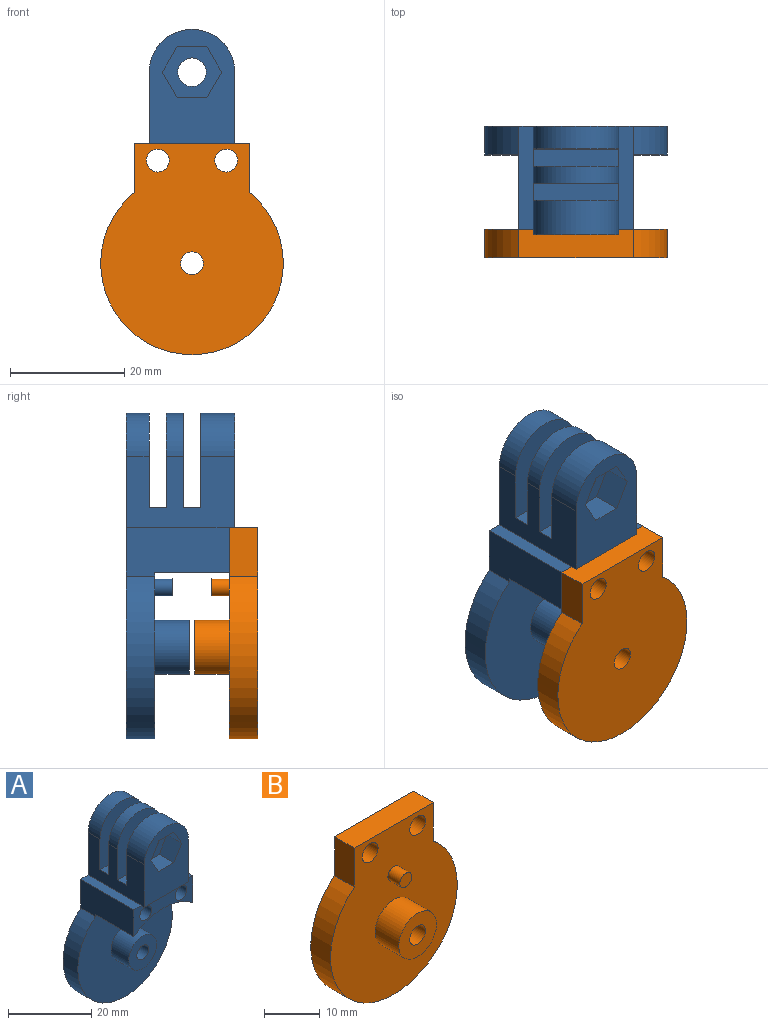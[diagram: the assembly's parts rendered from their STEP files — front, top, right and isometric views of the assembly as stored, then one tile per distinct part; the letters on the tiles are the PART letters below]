
ASSEMBLY  parts=2 mates=1
PART A: 39 faces, bbox 32x19x57 mm
  f0: cylinder r=2.5mm len=5mm, axis (0,-1,0), area 15.7mm2, adj f28,f32
  f1: plane 19x12.5mm, normal (1,0,0), area 183.5mm2, adj f3,f4,f5,f6,f10,f13,f23,f24
  f2: plane 19x12.5mm, normal (-1,0,0), area 183.5mm2, adj f3,f4,f5,f6,f7,f13,f23,f24
  f3: cylinder r=7.5mm len=15mm, axis (0,1,0), area 141.4mm2, adj f1,f2,f6,f28
  f4: cylinder r=7.5mm len=15mm, axis (0,1,0), area 70.7mm2, adj f1,f2,f26,f29
  f5: cylinder r=7.5mm len=15mm, axis (0,1,0), area 94.2mm2, adj f1,f2,f13,f25
  f6: plane 20x15mm, normal (0,-1,0), area 205.7mm2, adj f1,f2,f3,f23,f33,f34,f35,f36
  f7: plane 18x2.5mm, normal (0,0,1), area 45mm2, adj f2,f11,f13,f19
  f8: cylinder r=16mm len=32mm, axis (0,1,0), area 394.6mm2, adj f9,f11,f12,f13
  f9: plane 18x8.51mm, normal (1,0,0), area 144.9mm2, adj f8,f10,f12,f13,f18,f19
  f10: plane 18x2.5mm, normal (0,0,1), area 45mm2, adj f1,f9,f13,f19
  f11: plane 18x8.51mm, normal (-1,0,0), area 144.9mm2, adj f7,f8,f12,f13,f18,f19
  f12: plane 32.5x32mm, normal (0,-1,0), area 737.1mm2, adj f8,f9,f11,f14,f16,f18
  f13: plane 57x32mm, normal (0,1,0), area 1145mm2, adj f1,f2,f5,f7,f8,f9,f10,f11
  f14: cylinder r=1.5mm len=3mm, axis (0,1,0), area 28.3mm2, adj f12,f15
  f15: plane 3x3mm, normal (0,-1,0), area 7.1mm2, adj f14
  f16: cylinder r=4.75mm len=9.5mm, axis (0,1,0), area 179.1mm2, adj f12,f17
  f17: plane 9.5x9.5mm, normal (0,-1,0), area 58.3mm2, adj f16,f22
  f18: cylinder r=16.5mm len=20mm, axis (0,1,0), area 279.3mm2, adj f9,f11,f12,f19
  f19: plane 20x7.88mm, normal (0,-1,0), area 86.4mm2, adj f7,f9,f10,f11,f18,f20,f21,f23
  f20: cylinder r=2mm len=18mm, axis (0,-1,0), area 226.2mm2, adj f13,f19
  f21: cylinder r=2mm len=18mm, axis (0,-1,0), area 226.2mm2, adj f13,f19
  f22: cylinder r=2mm len=11mm, axis (0,-1,0), area 138.2mm2, adj f13,f17
  f23: plane 15x1mm, normal (0,0,-1), area 15mm2, adj f1,f2,f6,f19
  f24: plane 15x3mm, normal (0,0,1), area 45mm2, adj f1,f2,f25,f26
  f25: plane 16.5x15mm, normal (0,-1,0), area 203.7mm2, adj f1,f2,f5,f24,f31
  f26: plane 16.5x15mm, normal (0,1,0), area 203.7mm2, adj f1,f2,f4,f24,f30
  f27: plane 15x3mm, normal (0,0,1), area 45mm2, adj f1,f2,f28,f29
  f28: plane 16.5x15mm, normal (0,1,0), area 203.7mm2, adj f0,f1,f2,f3,f27
  f29: plane 16.5x15mm, normal (0,-1,0), area 203.7mm2, adj f1,f2,f4,f27,f30
  f30: cylinder r=2.5mm len=5mm, axis (0,-1,0), area 47.1mm2, adj f26,f29
  f31: cylinder r=2.5mm len=5mm, axis (0,-1,0), area 62.8mm2, adj f13,f25
  f32: plane 10.39x9mm, normal (0,-1,0), area 50.5mm2, adj f0,f33,f34,f35,f36,f37,f38
  f33: plane 5.2x5mm, normal (0,0,-1), area 26mm2, adj f6,f32,f34,f38
  f34: plane 5x4.5mm, normal (0.87,0,-0.5), area 26mm2, adj f6,f32,f33,f35
  f35: plane 5x4.5mm, normal (0.87,0,0.5), area 26mm2, adj f6,f32,f34,f36
  f36: plane 5.2x5mm, normal (0,0,1), area 26mm2, adj f6,f32,f35,f37
  f37: plane 5x4.5mm, normal (-0.87,0,0.5), area 26mm2, adj f6,f32,f36,f38
  f38: plane 5x4.5mm, normal (-0.87,0,-0.5), area 26mm2, adj f6,f32,f33,f37
PART B: 13 faces, bbox 32x11x37 mm
  f0: plane 8.51x5mm, normal (1,0,0), area 42.6mm2, adj f1,f5,f6,f7
  f1: plane 20x5mm, normal (0,0,1), area 100mm2, adj f0,f2,f6,f7
  f2: plane 8.51x5mm, normal (-1,0,0), area 42.6mm2, adj f1,f5,f6,f7
  f3: cylinder r=2mm len=5mm, axis (0,-1,0), area 62.8mm2, adj f6,f7
  f4: cylinder r=2mm len=5mm, axis (0,-1,0), area 62.8mm2, adj f6,f7
  f5: cylinder r=16mm len=32mm, axis (0,1,0), area 394.6mm2, adj f0,f2,f6,f7
  f6: plane 37x32mm, normal (0,-1,0), area 823.4mm2, adj f0,f1,f2,f3,f4,f5,f8,f10
  f7: plane 37x32mm, normal (0,1,0), area 888.8mm2, adj f0,f1,f2,f3,f4,f5,f12
  f8: cylinder r=1.5mm len=3mm, axis (0,1,0), area 28.3mm2, adj f6,f9
  f9: plane 3x3mm, normal (0,-1,0), area 7.1mm2, adj f8
  f10: cylinder r=4.75mm len=9.5mm, axis (0,1,0), area 179.1mm2, adj f6,f11
  f11: plane 9.5x9.5mm, normal (0,-1,0), area 58.3mm2, adj f10,f12
  f12: cylinder r=2mm len=11mm, axis (0,-1,0), area 138.2mm2, adj f7,f11
PLACE A t=(-60.21,-2.26,3.4)mm
PLACE B rot(axis=(0,0,-1),180deg) t=(-60.21,-25.26,3.4)mm
MATE fastened A.f21 <-> B.f3  axis (0,-1,0) through (-66.21,-20.26,21.4)mm
